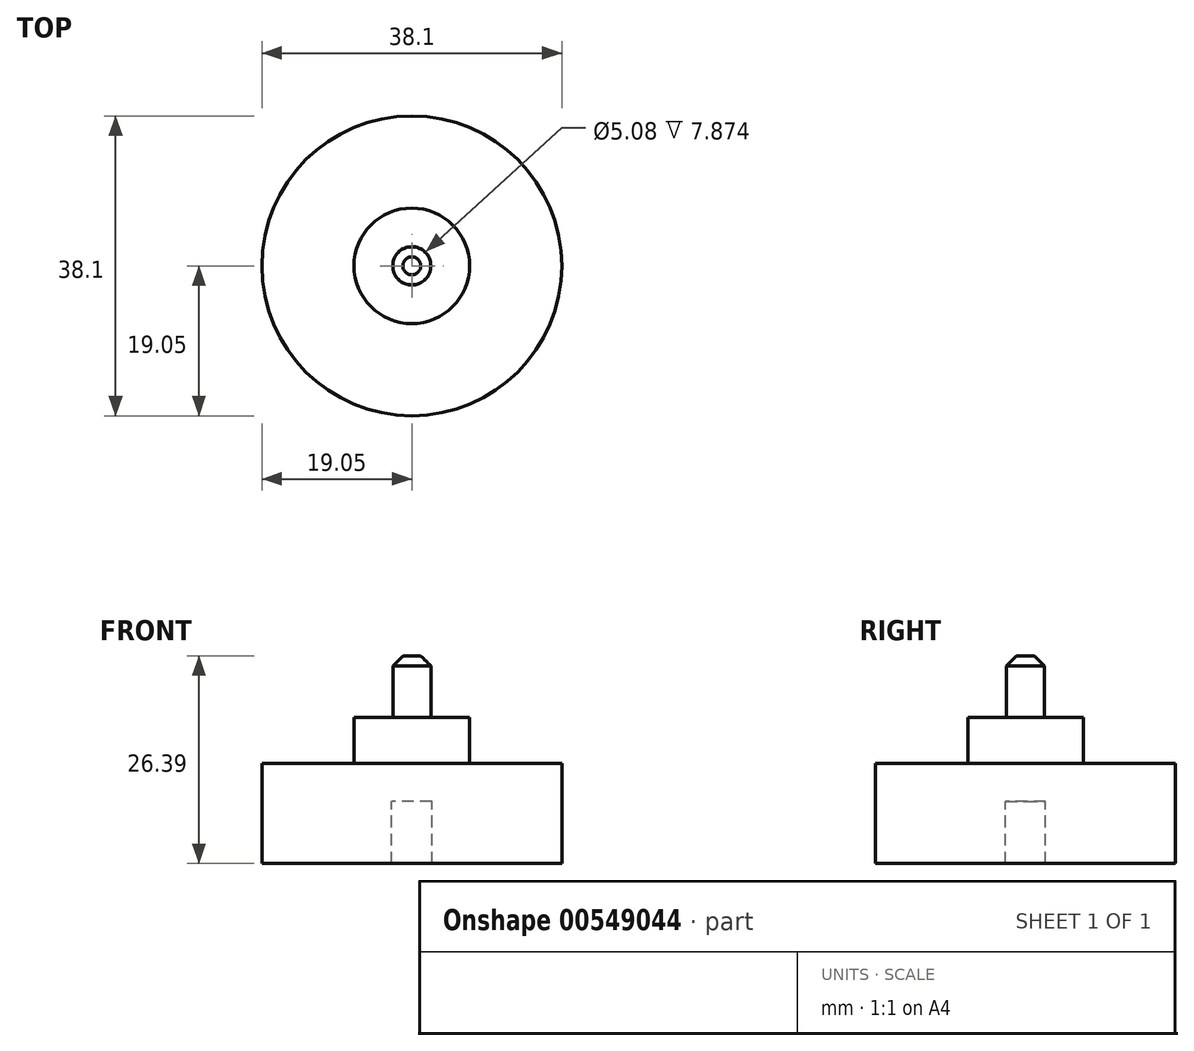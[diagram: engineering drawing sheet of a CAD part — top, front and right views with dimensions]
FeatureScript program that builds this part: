
annotation { "Feature Type Name" : "Feature", "Feature Type Description" : "" }
export const myFeature = defineFeature(function(context is Context, id is Id, definition is map)
    precondition{}
    {
        {
            var Q0;
            Q0=qCreatedBy(makeId("Front.planeOp"),FACE);
            var sketch = newSketch(context, id + "F0", { "sketchPlane" : qUnion([Q0])});
            skLineSegment(sketch, "E0", {"start": v(19.05, 0) * mm, "end": v(19.05, 12.7) * mm});
            skLineSegment(sketch, "E1", {"start": v(19.05, 12.7) * mm, "end": v(7.34, 12.7) * mm});
            skLineSegment(sketch, "E2", {"start": v(2.41, 18.54) * mm, "end": v(7.34, 18.54) * mm});
            skLineSegment(sketch, "E3", {"start": v(7.34, 18.54) * mm, "end": v(7.34, 12.7) * mm});
            skLineSegment(sketch, "E4", {"start": v(2.54, 0) * mm, "end": v(2.54, 7.87) * mm});
            skLineSegment(sketch, "E5", {"start": v(2.54, 7.87) * mm, "end": v(0, 7.87) * mm});
            skLineSegment(sketch, "E6", {"start": v(0, 26.4) * mm, "end": v(2.41, 26.4) * mm});
            skLineSegment(sketch, "E7", {"start": v(2.41, 26.4) * mm, "end": v(2.41, 18.54) * mm});
            skPoint(sketch, "E8.start.orphan", {"position": v(0, 18.54) * mm});
            skLineSegment(sketch, "E9", {"start": v(0, 26.4) * mm, "end": v(0, 7.87) * mm});
            skLineSegment(sketch, "E10", {"start": v(2.54, 0) * mm, "end": v(19.05, 0) * mm});
            skSolve(sketch);
        }
        {
            var Q0;
            Q0 = qSketchRegion(id + "F0", true);
            var Q1;
            Q1=sQuery(id+"F0.wireOp",EDGE,"E9");
            revolve(context, id + "F1", {"entities" : qUnion([Q0]), "axis" : qUnion([Q1]), "revolveType" : RevolveType.FULL});
        }
        {
            var Q0;
            Q0=makeQuery(id+"F1.opRevolve","SWEPT_EDGE",EDGE,{"disambiguationData":[OSD([sQuery(id+"F0.wireOp",EDGE,"E6"),sQuery(id+"F0.wireOp",EDGE,"E7")])]});
            chamfer(context, id + "F2", {"entities" : qUnion([Q0]), "width" : 1.27 * mm, "tangentPropagation" : true});
        }
    });
